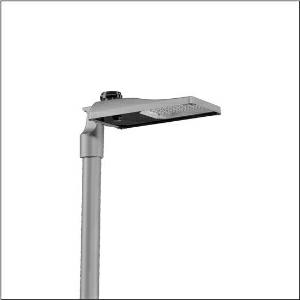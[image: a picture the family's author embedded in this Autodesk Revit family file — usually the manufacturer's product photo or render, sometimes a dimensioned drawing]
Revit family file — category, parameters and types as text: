
# Revit family: streetlight_sl_31_mini___st1_0a_5xh2d35m08ga_46b7
name_source: partatom
category: Lighting Fixtures
units: mm (PartAtom-declared; Revit-internal decimal feet)

## family parameters
Cut with Voids When Loaded = No
Host = Face
Light Source = No
Part Type = Normal
Room Calculation Point = No
Round Connector Dimension = Use Diameter
Shared = No

## types (1)
- --- (1 x LED, 5880 lm, 39.3 W, 3000K)
    Apparent Load = 39 VA
    CIE Flux Codes = 37 72 97 100 100
    Color Rendering = 70
    Color Temperature = 3000K
    Default Elevation = 1800 mm
    Description = Streetlight SL 31 mini NEMA (7pin), Desk-Remote mast luminaire for post-top, side-entry; light control with lens of PMMA; light distribution: ST1.0a, direct asymmetric distribution, for standard-compliant lighting for roads and squares; LED: luminous flux: 5.880lm, light colour: 730, colour temperature: 3000K; luminous efficacy: 149,6lm/W; control: pre-setting: linear dimming characteristic, flexible luminous flux parameterisation, time-dependent luminous flux control, constant luminous flux control, intelligent temperature release in ECG and LED module, overheat protection; luminaire housing, of diecast aluminium, Siteco® metallic grey (DB 702S), corrosivity category C5 high according to DIN EN ISO 12944; cover of toughened safety glass, transparent, mast flange of diecast aluminium, Siteco® metallic grey (DB 702S), spigot size: 76/60mm, mast flange included unmounted; with cable H07RN-F 3x 1.5mm², cable length: 6,5m, connection cable pre-assembled; mains connection: 220..240V, AC, 50/60Hz; power consumption (at start of service life): 39,3W / (at end of service life): 40,7W / (with reduced operation 50%): 18,1W; protection rating (complete): IP66; insulation class (complete): insulation class I (protective earthing); impact resistance: IK09; certification: CE, ENEC, ENEC+, VDE, UKCA; permissible operating ambient temperature for outdoor applications: -40..+50°C; packaging unit: 1 piece

Light Distribution: ST1.0a
    Height = 76 mm
    Lamp = 1 x LED
    Lamp Light Flux = 5880 lm
    Lamp Power = 39.3 W
    Lamp count = 1
    Length = 547 mm
    Luminous efficacy = 150 lm/W
    Manufacturer = Siteco
    ModVariant = No
    Model = 5XH2D35M08GA
    Number of Poles = 1
    OnlyDefault = Yes
    Power Factor = 1
    Product Name = Streetlight SL 31 mini | ST1.0a
    Product group = mast luminaire | pylon top
    ProductGroupID = 6100
    Protection Class = Protection class I
    Protection Degree = IP 66
    RLX_Detail_Level = 1
    RLX_Emergency_Light_Flux = 0 lm
    RLX_Emergency_Type = 0
    RLX_Emergency_Type_DB = No
    RlxData = <blob elided: 40353 chars, md5=e93201e5>
    Socket = socket
    Standby Power = 0 W
    System Light Flux = 5880 lm
    System Power = 39 W
    Type Comments = factory setting: luminous flux: 100 % | dim-lin: 254 | 798 mA
    Type Image = l_1300324.jpg
    URL = http://relux.com
    VarID = @adj_054468
    Voltage = 0 V
    Weight = 0.00 kg
    Width = 265 mm

## geometry (parser evidence)
native form markers: Blend x4, Sweep x11
no freeform markers — native parametric forms only
